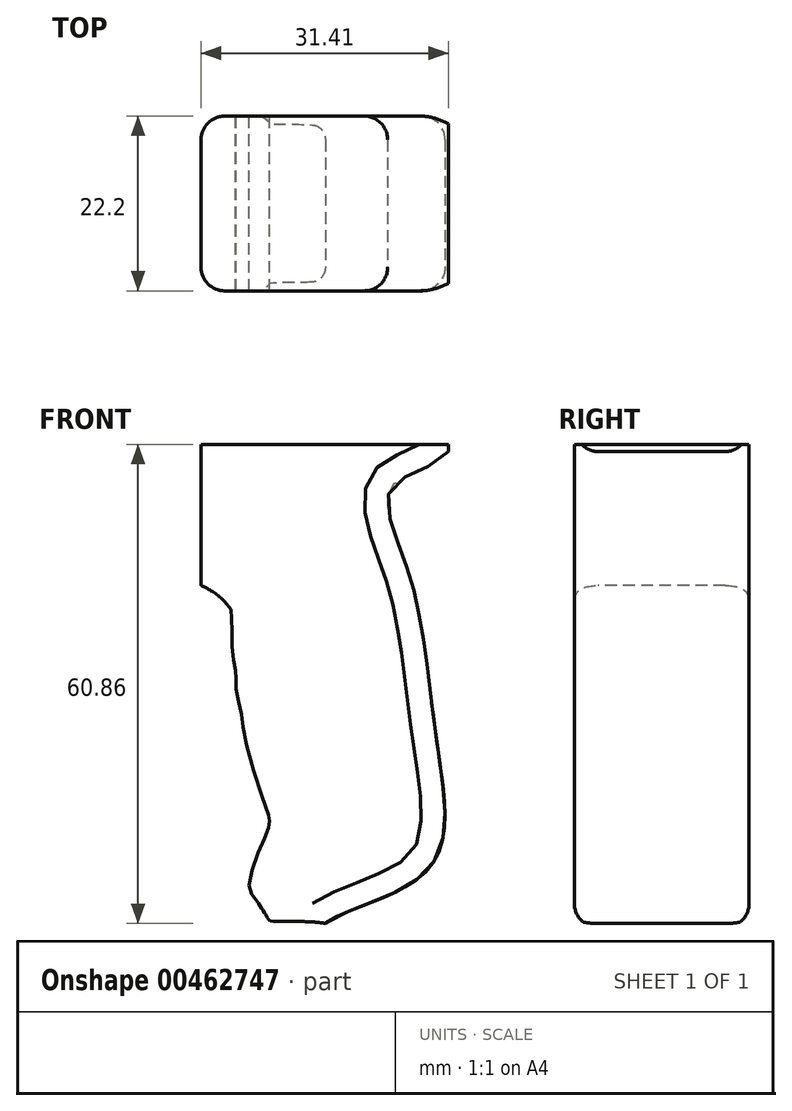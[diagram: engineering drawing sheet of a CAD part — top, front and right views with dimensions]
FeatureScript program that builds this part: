
annotation { "Feature Type Name" : "Feature", "Feature Type Description" : "" }
export const myFeature = defineFeature(function(context is Context, id is Id, definition is map)
    precondition{}
    {
        {
            var Q0;
            Q0=qCreatedBy(makeId("Front.planeOp"),FACE);
            var sketch = newSketch(context, id + "F0", { "sketchPlane" : qUnion([Q0])});
            skLineSegment(sketch, "E0.bottom", {"start": v(-3.16, 17.31) * mm, "end": v(28.25, 17.31) * mm});
            skLineSegment(sketch, "E0.top", {"start": v(-3.16, -44.03) * mm, "end": v(28.25, -44.03) * mm});
            skLineSegment(sketch, "E0.left", {"start": v(-3.16, 17.31) * mm, "end": v(-3.16, -44.03) * mm});
            skLineSegment(sketch, "E0.right", {"start": v(28.25, 17.31) * mm, "end": v(28.25, -44.03) * mm});
            skSolve(sketch);
        }
        {
            var Q0;
            Q0=makeQuery(id+"F0.imprint","IMPRINT",FACE,{"disambiguationData":[TD([[makeQuery(id+"F0.imprint","IMPRINT",EDGE,{"derivedFrom":sQuery(id+"F0.wireOp",EDGE,"E0.bottom")}),-1.0]])]});
            extrude(context, id + "F1", {"entities" : qUnion([Q0]), "endBound" : BoundingType.SYMMETRIC, "depth" : 22.2 * mm});
        }
        {
            var Q0;
            Q0=qCreatedBy(makeId("Front.planeOp"),FACE);
            var sketch = newSketch(context, id + "F2", { "sketchPlane" : qUnion([Q0])});
            skFitSpline(sketch, "E1", {"points": [v(11.56, -45.41) * mm, v(24.77, -37.58) * mm, v(26.88, -21.2) * mm, v(23.88, -1.31) * mm, v(21.07, 7.05) * mm, v(21.07, 11.98) * mm, v(25.9, 14.62) * mm, v(30.66, 16.3) * mm, v(35.33, -49.29) * mm, v(11.56, -45.41) * mm]});
            skSolve(sketch);
        }
        {
            var Q0;
            Q0=qCreatedBy(makeId("Front.planeOp"),FACE);
            var sketch = newSketch(context, id + "F3", { "sketchPlane" : qUnion([Q0])});
            skFitSpline(sketch, "E2", {"points": [v(14.22, -44.38) * mm, v(5.9, -43.25) * mm, v(5.24, -42.78) * mm, v(3.54, -40.22) * mm, v(2.91, -38.9) * mm, v(4.3, -34.08) * mm, v(5.45, -31.35) * mm, v(5.52, -30.52) * mm, v(5.45, -30.03) * mm, v(2.47, -20.45) * mm, v(1.88, -16.6) * mm, v(1.25, -13.63) * mm, v(1.3, -12) * mm, v(0.97, -10.3) * mm, v(0.75, -6.78) * mm, v(0.69, -4.04) * mm, v(0.2, -3.04) * mm, v(-7.07, -0.87) * mm, v(-6.51, -48.8) * mm, v(14.22, -44.38) * mm]});
            skSolve(sketch);
        }
        {
            var Q0;
            Q0 = qSketchRegion(id + "F2", true);
            extrude(context, id + "F4", {"entities" : qUnion([Q0]), "operationType" : NewBodyOperationType.REMOVE, "endBound" : BoundingType.SYMMETRIC, "oppositeDirection" : true, "depth" : 25 * mm});
        }
        {
            var Q0;
            Q0=makeQuery(id+"F4.boolean.opBoolean","INTERSECT",EDGE,{"derivedFrom":[makeQuery(id+"F1.opExtrude","CAP_FACE",FACE,{"disambiguationData":[OSD([sQuery(id+"F0.wireOp",EDGE,"E0.bottom"),sQuery(id+"F0.wireOp",EDGE,"E0.top"),sQuery(id+"F0.wireOp",EDGE,"E0.left"),sQuery(id+"F0.wireOp",EDGE,"E0.right")])],"isStart":false}),makeQuery(id+"F4.opExtrude","SWEPT_FACE",FACE,{"disambiguationData":[OSD([sQuery(id+"F2.wireOp",EDGE,"E1")])]})]});
            var Q1;
            Q1=makeQuery(id+"F4.boolean.opBoolean","INTERSECT",EDGE,{"derivedFrom":[makeQuery(id+"F1.opExtrude","CAP_FACE",FACE,{"disambiguationData":[OSD([sQuery(id+"F0.wireOp",EDGE,"E0.bottom"),sQuery(id+"F0.wireOp",EDGE,"E0.top"),sQuery(id+"F0.wireOp",EDGE,"E0.left"),sQuery(id+"F0.wireOp",EDGE,"E0.right")])],"isStart":true}),makeQuery(id+"F4.opExtrude","SWEPT_FACE",FACE,{"disambiguationData":[OSD([sQuery(id+"F2.wireOp",EDGE,"E1")])]})]});
            var Q2;
            Q2=makeQuery(id+"F1.opExtrude","CAP_EDGE",EDGE,{"disambiguationData":[OSD([sQuery(id+"F0.wireOp",EDGE,"E0.top")])],"isStart":false});
            var Q3;
            Q3=makeQuery(id+"F1.opExtrude","CAP_EDGE",EDGE,{"disambiguationData":[OSD([sQuery(id+"F0.wireOp",EDGE,"E0.left")])],"isStart":false});
            var Q4;
            Q4=makeQuery(id+"F1.opExtrude","CAP_EDGE",EDGE,{"disambiguationData":[OSD([sQuery(id+"F0.wireOp",EDGE,"E0.left")])],"isStart":true});
            var Q5;
            Q5=makeQuery(id+"F1.opExtrude","CAP_EDGE",EDGE,{"disambiguationData":[OSD([sQuery(id+"F0.wireOp",EDGE,"E0.top")])],"isStart":true});
            var Q6;
            Q6=makeQuery(id+"F1.opExtrude","SWEPT_EDGE",EDGE,{"disambiguationData":[OSD([sQuery(id+"F0.wireOp",EDGE,"E0.top"),sQuery(id+"F0.wireOp",EDGE,"E0.left")])]});
            var Q7;
            Q7=makeQuery(id+"F4.boolean.opBoolean","INTERSECT",EDGE,{"derivedFrom":[makeQuery(id+"F1.opExtrude","SWEPT_FACE",FACE,{"disambiguationData":[OSD([sQuery(id+"F0.wireOp",EDGE,"E0.top")])]}),makeQuery(id+"F4.opExtrude","SWEPT_FACE",FACE,{"disambiguationData":[OSD([sQuery(id+"F2.wireOp",EDGE,"E1")])]})]});
            fillet(context, id + "F5", {"entities" : qUnion([Q0, Q1, Q2, Q3, Q4, Q5, Q6, Q7]), "radius" : 3 * mm, "tangentPropagation" : true, "allowEdgeOverflow" : false});
        }
        {
            var Q0;
            Q0 = qSketchRegion(id + "F3", true);
            extrude(context, id + "F6", {"entities" : qUnion([Q0]), "operationType" : NewBodyOperationType.REMOVE, "endBound" : BoundingType.SYMMETRIC, "oppositeDirection" : true, "depth" : 25 * mm});
        }
    });
